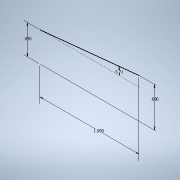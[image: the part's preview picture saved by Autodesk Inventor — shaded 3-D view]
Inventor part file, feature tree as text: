
AUTODESK INVENTOR PART (.ipt)
format: ipt  version: 2020.3 (Build 243373000, 373)  size: 88,064 bytes
history: native  units: in
note: dims shown in document units (in); Inventor stores cm internally (conversion verified against a paired STEP export)
features: sketch x1
ambient origin geometry x8: Origin, YZ Plane, XZ Plane, XY Plane, X Axis, Y Axis, Z Axis, Center Point
feature tree (1):
  sketch  "Sketch1"  dims[d0=0.45in d1=0.6in d2=1.5in d3=0.0392in]
